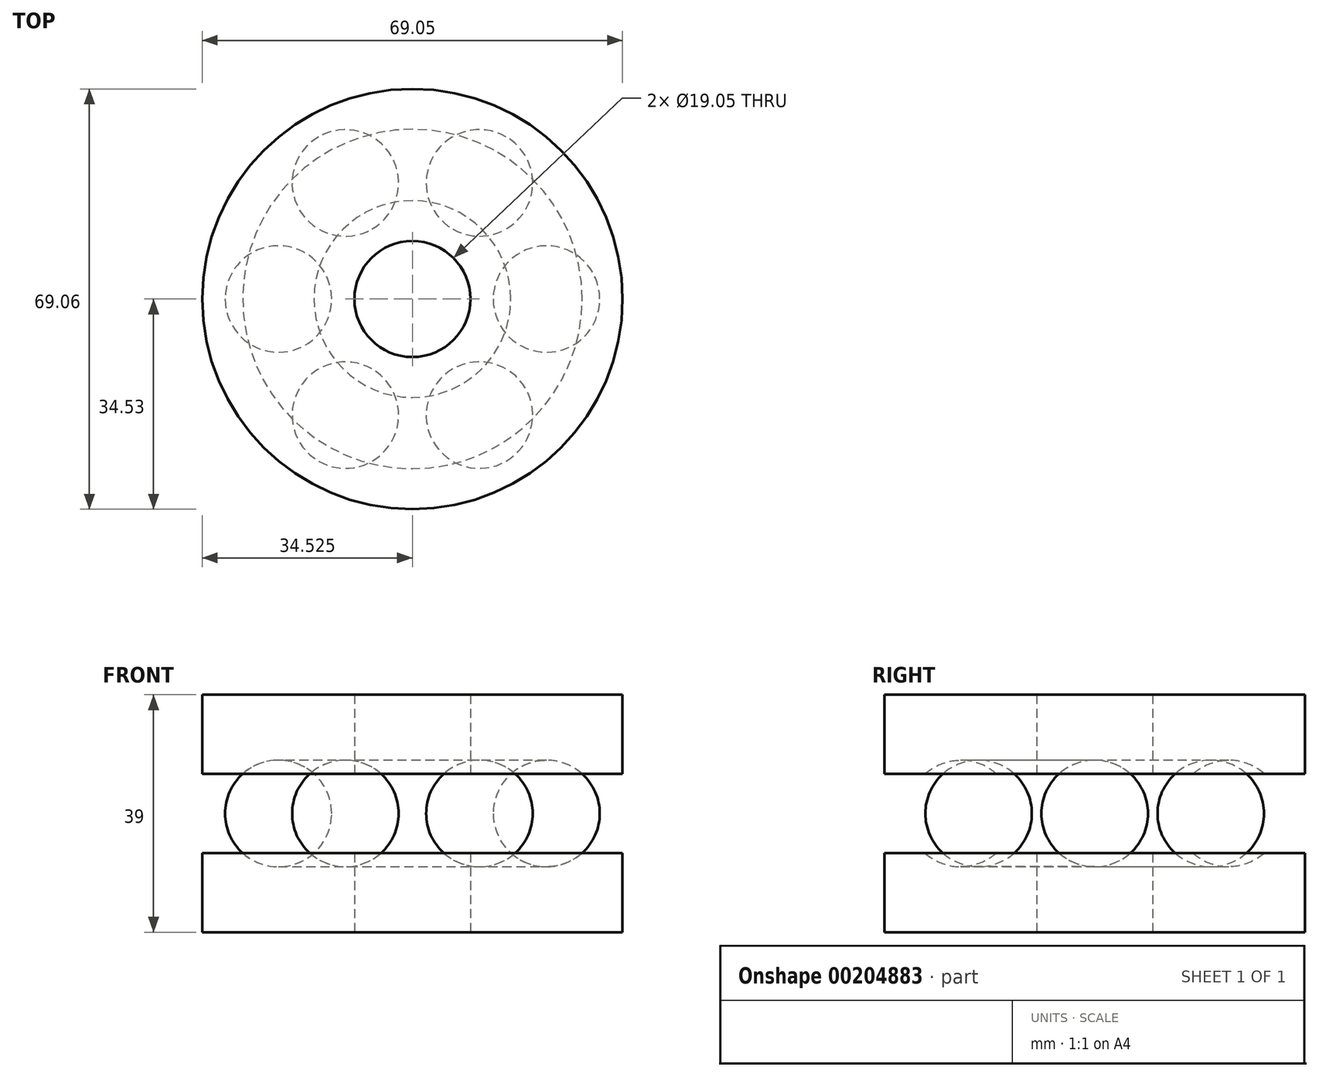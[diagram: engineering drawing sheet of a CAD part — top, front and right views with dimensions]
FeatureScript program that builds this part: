
annotation { "Feature Type Name" : "Feature", "Feature Type Description" : "" }
export const myFeature = defineFeature(function(context is Context, id is Id, definition is map)
    precondition{}
    {
        {
            var Q0;
            Q0=qCreatedBy(makeId("Front.planeOp"),FACE);
            var sketch = newSketch(context, id + "F0", { "sketchPlane" : qUnion([Q0])});
            skLineSegment(sketch, "E0.bottom", {"start": v(0, 0) * mm, "end": v(25, 0) * mm});
            skLineSegment(sketch, "E0.top", {"start": v(0, 13) * mm, "end": v(6.64, 13) * mm});
            skLineSegment(sketch, "E0.left", {"start": v(0, 0) * mm, "end": v(0, 13) * mm});
            skLineSegment(sketch, "E0.right", {"start": v(25, 0) * mm, "end": v(25, 13) * mm});
            skLineSegment(sketch, "E1", {"start": v(-9.53, 0) * mm, "end": v(-9.53, 28.75) * mm});
            skArc(sketch, "E2", {"start": v(6.64, 13) * mm, "mid": v(12.5, 10.75) * mm, "end": v(18.36, 13) * mm});
            skPoint(sketch, "E2.centerSnap0", {"position": v(12.5, 13) * mm});
            skLineSegment(sketch, "E3.trimOffspring", {"start": v(18.36, 13) * mm, "end": v(25, 13) * mm});
            skSolve(sketch);
        }
        {
            var Q0;
            Q0=makeQuery(id+"F0.imprint","IMPRINT",FACE,{"disambiguationData":[TD([[makeQuery(id+"F0.imprint","IMPRINT",EDGE,{"derivedFrom":sQuery(id+"F0.wireOp",EDGE,"E0.bottom")}),1.0]])]});
            var Q1;
            Q1=sQuery(id+"F0.wireOp",EDGE,"E1");
            revolve(context, id + "F1", {"entities" : qUnion([Q0]), "axis" : qUnion([Q1]), "revolveType" : RevolveType.FULL});
        }
        {
            var Q0;
            Q0=qCreatedBy(makeId("Front.planeOp"),FACE);
            var sketch = newSketch(context, id + "F2", { "sketchPlane" : qUnion([Q0])});
            skArc(sketch, "E4", {"start": v(3.75, 19.5) * mm, "mid": v(12.5, 10.75) * mm, "end": v(21.25, 19.5) * mm});
            skLineSegment(sketch, "E5", {"start": v(3.75, 19.5) * mm, "end": v(21.25, 19.5) * mm});
            skSolve(sketch);
        }
        {
            var Q0;
            Q0=makeQuery(id+"F2.imprint","IMPRINT",FACE,{"disambiguationData":[TD([[makeQuery(id+"F2.imprint","IMPRINT",EDGE,{"derivedFrom":sQuery(id+"F2.wireOp",EDGE,"E4")}),1.0]])]});
            var Q1;
            Q1=sQuery(id+"F2.wireOp",EDGE,"E5");
            revolve(context, id + "F3", {"operationType" : NewBodyOperationType.ADD, "entities" : qUnion([Q0]), "axis" : qUnion([Q1]), "revolveType" : RevolveType.FULL});
        }
        {
            var Q0;
            Q0=makeQuery(id+"F3.opRevolve","SWEPT_BODY",BODY,{"disambiguationData":[OSD([sQuery(id+"F2.wireOp",EDGE,"E4"),sQuery(id+"F2.wireOp",EDGE,"E5")])]});
            var Q1;
            Q1=makeQuery(id+"F1.opRevolve","SWEPT_FACE",FACE,{"disambiguationData":[OSD([sQuery(id+"F0.wireOp",EDGE,"E0.left")])]});
            circularPattern(context, id + "F4", {"entities" : qUnion([Q0]), "axis" : qUnion([Q1]), "angle" : 360 * degree, "instanceCount" : 6, "equalSpace" : true});
        }
        {
            var Q0;
            Q0=qCreatedBy(makeId("Front.planeOp"),FACE);
            var sketch = newSketch(context, id + "F5", { "sketchPlane" : qUnion([Q0])});
            skLineSegment(sketch, "E6", {"start": v(-9.52, 0) * mm, "end": v(-9.53, 41.16) * mm});
            skLineSegment(sketch, "E7.bottom", {"start": v(0, 26) * mm, "end": v(6.64, 26) * mm});
            skLineSegment(sketch, "E7.left", {"start": v(0, 26) * mm, "end": v(0, 39) * mm});
            skLineSegment(sketch, "E7.right", {"start": v(25, 26) * mm, "end": v(25, 39) * mm});
            skArc(sketch, "E8", {"start": v(18.36, 26) * mm, "mid": v(12.5, 28.25) * mm, "end": v(6.64, 26) * mm});
            skPoint(sketch, "E8.centerSnap0", {"position": v(12.5, 26) * mm});
            skLineSegment(sketch, "E9", {"start": v(0, 39) * mm, "end": v(25, 39) * mm});
            skLineSegment(sketch, "E10.trimOffspring", {"start": v(18.36, 26) * mm, "end": v(25, 26) * mm});
            skSolve(sketch);
        }
        {
            var Q0;
            Q0=makeQuery(id+"F5.imprint","IMPRINT",FACE,{"disambiguationData":[TD([[makeQuery(id+"F5.imprint","IMPRINT",EDGE,{"derivedFrom":sQuery(id+"F5.wireOp",EDGE,"E7.bottom")}),1.0]])]});
            var Q1;
            Q1=sQuery(id+"F5.wireOp",EDGE,"E6");
            revolve(context, id + "F6", {"entities" : qUnion([Q0]), "axis" : qUnion([Q1]), "revolveType" : RevolveType.FULL});
        }
    });
